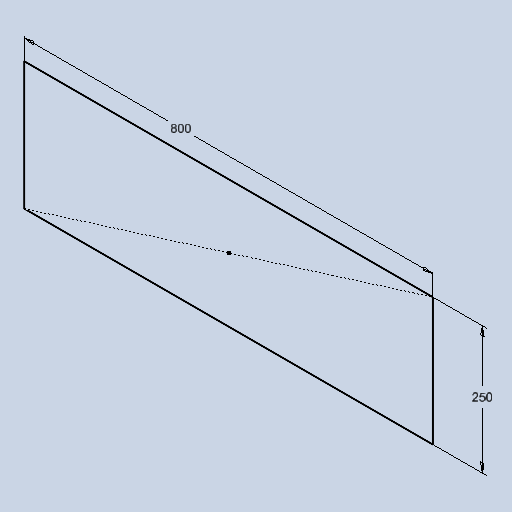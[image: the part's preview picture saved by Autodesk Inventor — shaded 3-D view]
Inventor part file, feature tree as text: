
AUTODESK INVENTOR PART (.ipt)
format: ipt  version: 2025 (Build 290162010, 162A)  size: 126,976 bytes
history: native  units: mm
features: sketch x1
ambient origin geometry x8: Origin, YZ Plane, XZ Plane, XY Plane, X Axis, Y Axis, Z Axis, Center Point
feature tree (1):
  sketch  "Sketch1"  dims[d0=800.0mm d1=250.0mm]
